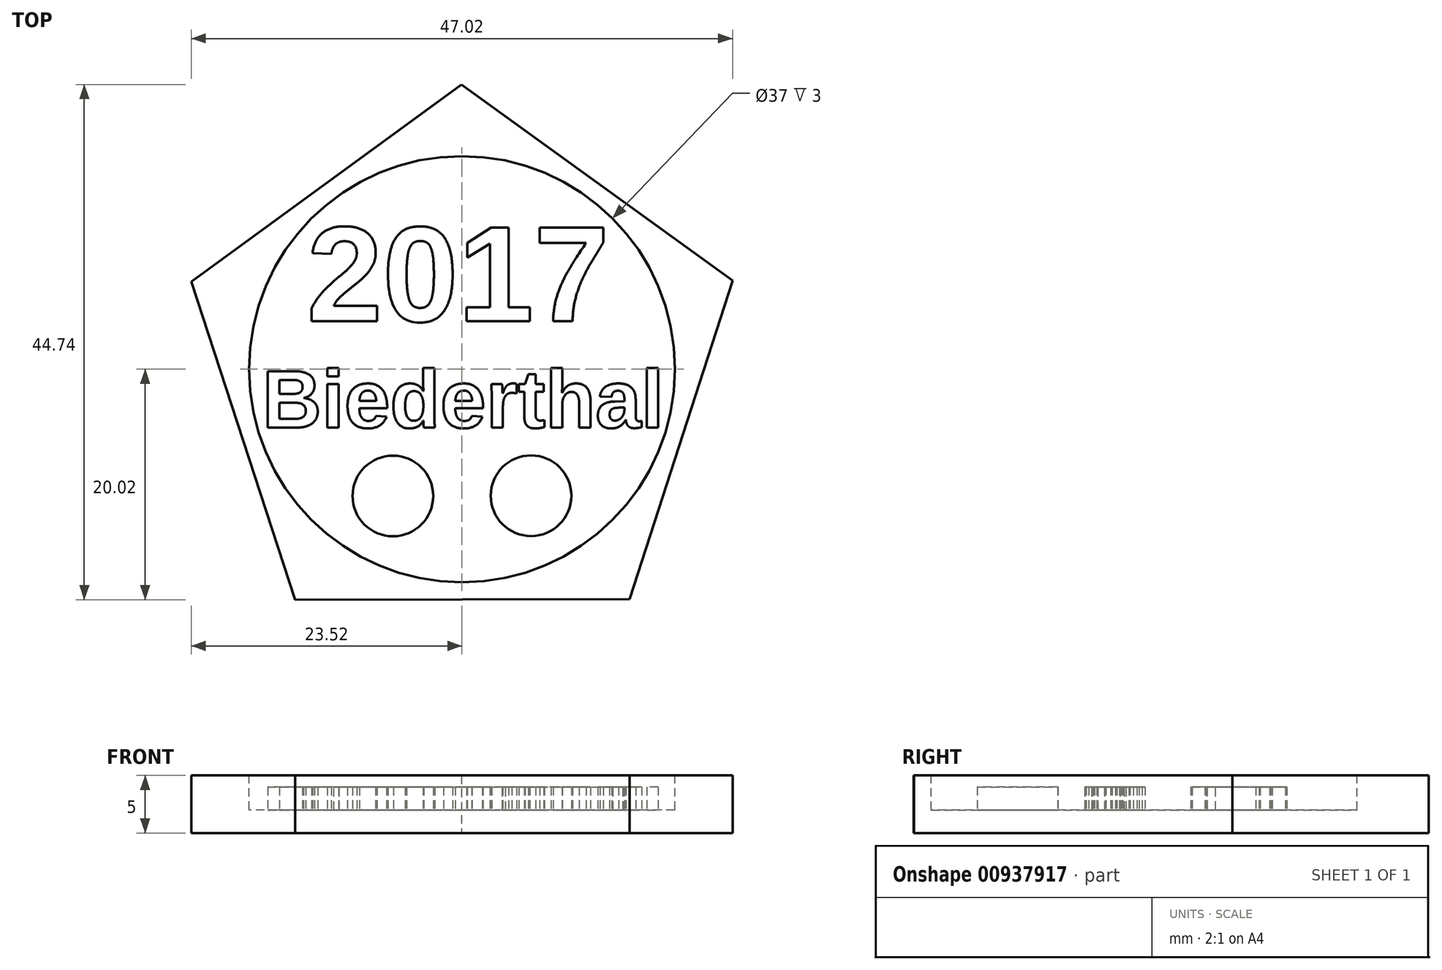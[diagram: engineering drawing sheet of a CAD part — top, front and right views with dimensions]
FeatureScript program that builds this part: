
annotation { "Feature Type Name" : "Feature", "Feature Type Description" : "" }
export const myFeature = defineFeature(function(context is Context, id is Id, definition is map)
    precondition{}
    {
        {
            var Q0;
            Q0=qCreatedBy(makeId("Top.planeOp"),FACE);
            var sketch = newSketch(context, id + "F0", { "sketchPlane" : qUnion([Q0])});
            skCircle(sketch, "E0.cCircle", {"center": v(0, 0) * mm, "radius": 20 * mm, "construction": true});
            skLineSegment(sketch, "E0.0", {"start": v(-23.52, 7.6) * mm, "end": v(-0.04, 24.72) * mm});
            skLineSegment(sketch, "E0.1", {"start": v(-0.04, 24.72) * mm, "end": v(23.5, 7.68) * mm});
            skLineSegment(sketch, "E0.2", {"start": v(23.5, 7.68) * mm, "end": v(14.56, -19.98) * mm});
            skLineSegment(sketch, "E0.3", {"start": v(14.56, -19.98) * mm, "end": v(-14.5, -20.02) * mm});
            skLineSegment(sketch, "E0.4", {"start": v(-14.5, -20.02) * mm, "end": v(-23.52, 7.6) * mm});
            skPoint(sketch, "E0.0.midPoint", {"position": v(-11.78, 16.16) * mm});
            skSolve(sketch);
        }
        {
            var Q0;
            Q0=qSketchRegion(id+"F0",true);
            extrude(context, id + "F1", {"entities" : qUnion([Q0]), "depth" : 5 * mm, "offsetDistance" : 25 * mm});
        }
        {
            var Q0;
            Q0=makeQuery(id+"F1.opExtrude","CAP_FACE",FACE,{"disambiguationData":[OSD([sQuery(id+"F0.wireOp",EDGE,"E0.0"),sQuery(id+"F0.wireOp",EDGE,"E0.1"),sQuery(id+"F0.wireOp",EDGE,"E0.2"),sQuery(id+"F0.wireOp",EDGE,"E0.3"),sQuery(id+"F0.wireOp",EDGE,"E0.4")])],"isStart":false});
            var sketch = newSketch(context, id + "F2", { "sketchPlane" : qUnion([Q0])});
            skCircle(sketch, "E1", {"center": v(0, 0) * mm, "radius": 18.5 * mm});
            skSolve(sketch);
        }
        {
            var Q0;
            {var subQ0=sQuery(id+"F2.wireOp",EDGE,"E1");var subQ4=makeQuery(id+"F2.imprint","INTERSECT",VERTEX,{"derivedFrom":[makeQuery(id+"F1.opExtrude","CAP_EDGE",EDGE,{"disambiguationData":[OSD([sQuery(id+"F0.wireOp",EDGE,"E0.0")])],"isStart":false}),subQ0]});Q0=makeQuery(id+"F2.imprint","IMPRINT",FACE,{"disambiguationData":[TD([[makeQuery(id+"F2.imprint","IMPRINT",EDGE,{"disambiguationData":[TD([[subQ4,1.0]])],"derivedFrom":subQ0}),1.0]])]});}
            extrude(context, id + "F3", {"entities" : qUnion([Q0]), "operationType" : NewBodyOperationType.REMOVE, "oppositeDirection" : true, "depth" : 3 * mm, "offsetDistance" : 25 * mm});
        }
        {
            var Q0;
            Q0=makeQuery(id+"F3.boolean.opBoolean","COPY",FACE,{"derivedFrom":makeQuery(id+"F3.opExtrude","CAP_FACE",FACE,{"disambiguationData":[OSD([sQuery(id+"F2.wireOp",EDGE,"E1")])],"isStart":false})});
            var sketch = newSketch(context, id + "F4", { "sketchPlane" : qUnion([Q0])});
            skText(sketch, "E2", { "text": "2017", "fontName": "Arimo-Bold.ttf"});
            skText(sketch, "E3", { "text": "Biederthal", "fontName": "Arimo-Bold.ttf"});
            skCircle(sketch, "E4", {"center": v(-6, -11) * mm, "radius": 3.5 * mm});
            skCircle(sketch, "E5", {"center": v(6, -11) * mm, "radius": 3.5 * mm});
            const initialGuessF4  = {"E2": [-0.01346, 0.00416, 1, 0, 0.0085], "E3": [-0.01736, -0.00508, 1, 0, 0.00514]};
            skSetInitialGuess(sketch, initialGuessF4);
            skSolve(sketch);
        }
        {
            var Q0;
            Q0=qSketchRegion(id+"F4",true);
            extrude(context, id + "F5", {"entities" : qUnion([Q0]), "operationType" : NewBodyOperationType.ADD, "depth" : 2 * mm, "offsetDistance" : 25 * mm});
        }
    });
